# Revit family: Shower_Wall_Nero_SwivelArm_250mmHead
name_source: partatom
category: Plumbing Fixtures
units: mm (PartAtom-declared; Revit-internal decimal feet)

## family parameters
Always vertical = Yes
Cut with Voids When Loaded = Yes
OmniClass Number = 23.31.11.19
Part Type = Normal
Room Calculation Point = No
Round Connector Dimension = Use Diameter
Shared = No
Work Plane-Based = No

## types (5) — shared parameters
Assembly Code = C1030210
CW Connection = Yes
HW Connection = Yes
IfcExportAs = IfcSanitaryTerminal
IfcExportType = SHOWER
Manufacturer = Nero
ManufacturerOverallDepth = 469 mm
ManufacturerOverallHeight = 347.5 mm
ManufacturerOverallWidth = 250 mm  [stored 0.82021 ft]
ManufacturerURLProductSpecific = https://nerotapware.com.au
ModifiedIssue = 20231106 $
URL = https://nerotapware.com.au
Uniclass2015Code = Pr_40_20_87_75
Uniclass2015Title = Shower fittings package
Uniclass2015Version = Products v1.28
Vent Connection = No
Waste Connection = No
zero-valued in all types: Default Elevation

## per-type parameters (varying)
| type | BodyMaterial | Description | ManufacturerSpecCode | Model | Type Comments |
| Gunmetal (NR506GM + NRROA1001GM) | Metal_GunMetal_Nero | 250Mm Round Shower Head Gunmetal With Round Swivel Shower Arm | NR506GM + NRROA1001GM | NR506GM + NRROA1001GM | Shower - Wall - Round Arm - 230mm Head Air Shower Gunmetal |
| Brushed Gold (NR506BG + NRROA1001BG) | Metal_Gold_Nero_Brushed | 250Mm Round Shower Head Brushed Gold With Round Swivel Shower Arm | NR506BG + NRROA1001BG | NR506BG + NRROA1001BG | Shower - Wall - Round Arm - 230mm Head Air Shower Brushed Gold |
| Brushed Nickel (NR506BN + NRROA1001BN) | Metal_Nickel_Nero_Brushed | 250Mm Round Shower Head Brushed Nickel With Round Swivel Shower Arm | NR506BN + NRROA1001BN | NR506BN + NRROA1001BN | Shower - Wall - Round Arm - 230mm Head Air Shower Brushed Nickel |
| Matte Black (NR506MB + NRROA1001MB) | Metal_MatteBlack_Nero | 250Mm Round Shower Head Matte Black With Round Swivel Shower Arm | NR506MB + NRROA1001MB | NR506MB + NRROA1001MB | Shower - Wall - Round Arm - 230mm Head Air Shower Matte Black |
| Chrome (NR506CH + NRROA1001CH) | Metal_Chrome_Nero | 250Mm Round Shower Head Chrome With Round Swivel Shower Arm | NR506CH + NRROA1001CH | NR506CH + NRROA1001CH | Shower - Wall - Round Arm - 230mm Head Air Shower Chrome |

note: [stored X ft] marks values corroborated as IEEE doubles in the binary element streams (Revit-internal decimal feet)

## geometry (parser evidence)
native form markers: Sweep x1
no freeform markers — native parametric forms only
